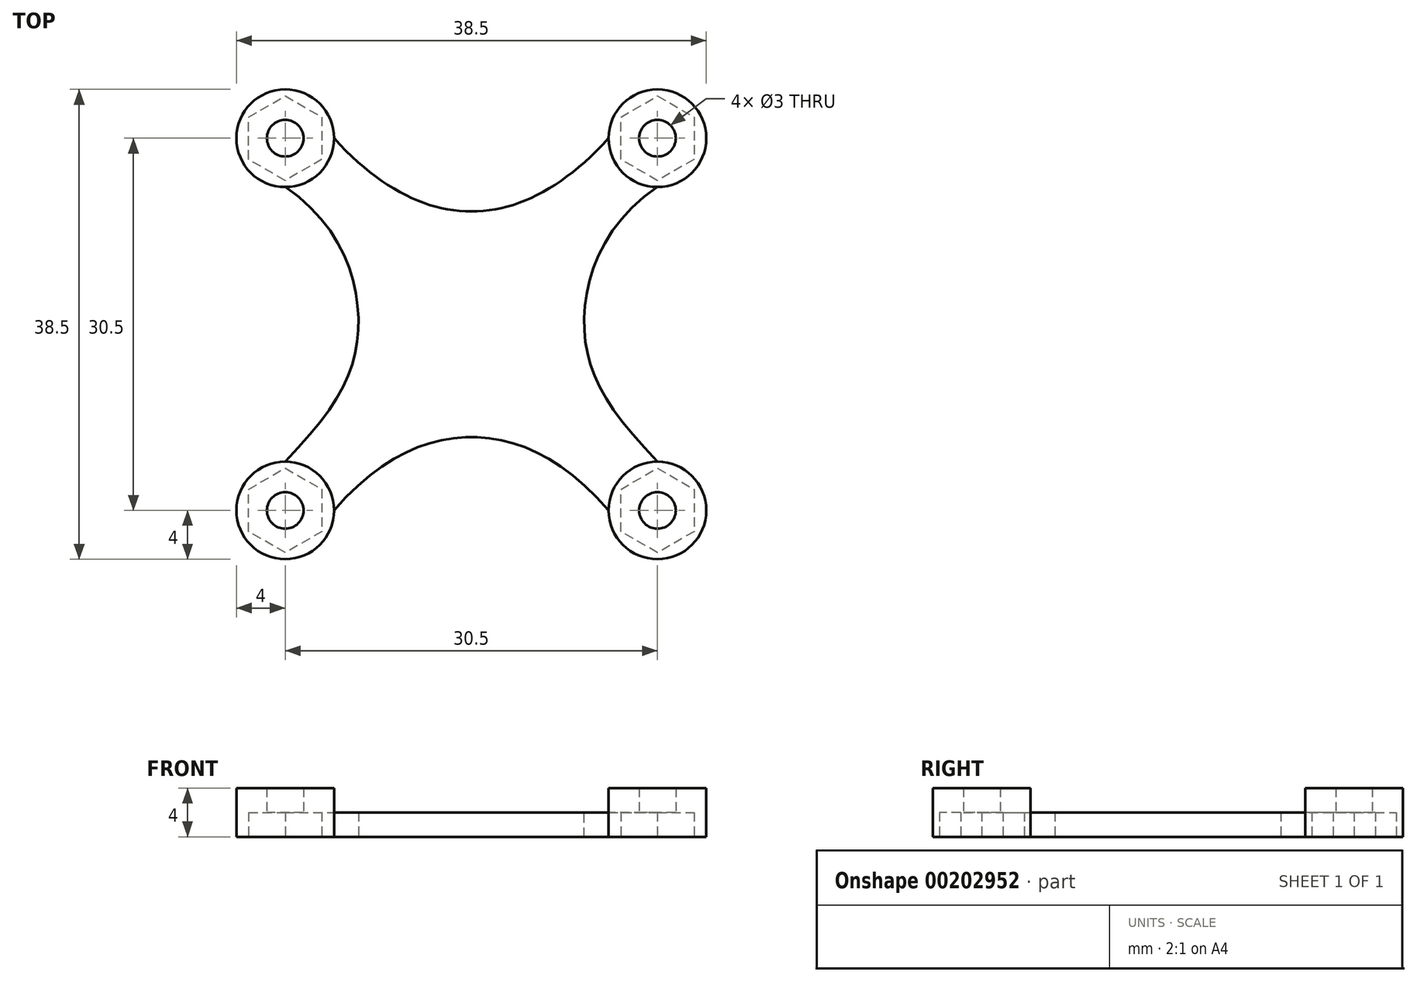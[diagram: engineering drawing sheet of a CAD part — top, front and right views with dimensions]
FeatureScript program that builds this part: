
annotation { "Feature Type Name" : "Feature", "Feature Type Description" : "" }
export const myFeature = defineFeature(function(context is Context, id is Id, definition is map)
    precondition{}
    {
        {
            var Q0;
            Q0=qCreatedBy(makeId("Top.planeOp"),FACE);
            var sketch = newSketch(context, id + "F0", { "sketchPlane" : qUnion([Q0])});
            skCircle(sketch, "E0", {"center": v(0, 0) * mm, "radius": 1.5 * mm});
            skCircle(sketch, "E1.0.1.0", {"center": v(0, 30.5) * mm, "radius": 1.5 * mm});
            skCircle(sketch, "E1.1.0.0", {"center": v(30.5, 0) * mm, "radius": 1.5 * mm});
            skCircle(sketch, "E1.1.1.0", {"center": v(30.5, 30.5) * mm, "radius": 1.5 * mm});
            skCircle(sketch, "E2", {"center": v(0, 0) * mm, "radius": 4 * mm});
            skCircle(sketch, "E3.0.1.0", {"center": v(0, 30.5) * mm, "radius": 4 * mm});
            skCircle(sketch, "E3.1.0.0", {"center": v(30.5, 0) * mm, "radius": 4 * mm});
            skCircle(sketch, "E3.1.1.0", {"center": v(30.5, 30.5) * mm, "radius": 4 * mm});
            skCircle(sketch, "E4.cCircle", {"center": v(0, 0) * mm, "radius": 3 * mm});
            skLineSegment(sketch, "E4.0", {"start": v(3, 1.73) * mm, "end": v(3, -1.73) * mm});
            skLineSegment(sketch, "E4.1", {"start": v(3, -1.73) * mm, "end": v(0, -3.46) * mm});
            skLineSegment(sketch, "E4.2", {"start": v(0, -3.46) * mm, "end": v(-3, -1.73) * mm});
            skLineSegment(sketch, "E4.3", {"start": v(-3, -1.73) * mm, "end": v(-3, 1.73) * mm});
            skLineSegment(sketch, "E4.4", {"start": v(-3, 1.73) * mm, "end": v(0, 3.46) * mm});
            skLineSegment(sketch, "E4.5", {"start": v(0, 3.46) * mm, "end": v(3, 1.73) * mm});
            skPoint(sketch, "E4.0.midPoint", {"position": v(3, 0) * mm});
            skLineSegment(sketch, "E5.0.1.0", {"start": v(0, 33.96) * mm, "end": v(3, 32.23) * mm});
            skLineSegment(sketch, "E5.0.1.1", {"start": v(3, 32.23) * mm, "end": v(3, 28.77) * mm});
            skLineSegment(sketch, "E5.0.1.2", {"start": v(3, 28.77) * mm, "end": v(0, 27.04) * mm});
            skLineSegment(sketch, "E5.0.1.3", {"start": v(0, 27.04) * mm, "end": v(-3, 28.77) * mm});
            skLineSegment(sketch, "E5.0.1.4", {"start": v(-3, 28.77) * mm, "end": v(-3, 32.23) * mm});
            skLineSegment(sketch, "E5.0.1.5", {"start": v(-3, 32.23) * mm, "end": v(0, 33.96) * mm});
            skLineSegment(sketch, "E5.1.0.0", {"start": v(30.5, 3.46) * mm, "end": v(33.5, 1.73) * mm});
            skLineSegment(sketch, "E5.1.0.1", {"start": v(33.5, 1.73) * mm, "end": v(33.5, -1.73) * mm});
            skLineSegment(sketch, "E5.1.0.2", {"start": v(33.5, -1.73) * mm, "end": v(30.5, -3.46) * mm});
            skLineSegment(sketch, "E5.1.0.3", {"start": v(30.5, -3.46) * mm, "end": v(27.5, -1.73) * mm});
            skLineSegment(sketch, "E5.1.0.4", {"start": v(27.5, -1.73) * mm, "end": v(27.5, 1.73) * mm});
            skLineSegment(sketch, "E5.1.0.5", {"start": v(27.5, 1.73) * mm, "end": v(30.5, 3.46) * mm});
            skLineSegment(sketch, "E5.1.1.0", {"start": v(30.5, 33.96) * mm, "end": v(33.5, 32.23) * mm});
            skLineSegment(sketch, "E5.1.1.1", {"start": v(33.5, 32.23) * mm, "end": v(33.5, 28.77) * mm});
            skLineSegment(sketch, "E5.1.1.2", {"start": v(33.5, 28.77) * mm, "end": v(30.5, 27.04) * mm});
            skLineSegment(sketch, "E5.1.1.3", {"start": v(30.5, 27.04) * mm, "end": v(27.5, 28.77) * mm});
            skLineSegment(sketch, "E5.1.1.4", {"start": v(27.5, 28.77) * mm, "end": v(27.5, 32.23) * mm});
            skLineSegment(sketch, "E5.1.1.5", {"start": v(27.5, 32.23) * mm, "end": v(30.5, 33.96) * mm});
            skFitSpline(sketch, "E6", {"points": [v(0, 26.5) * mm, v(6, 15.25) * mm, v(0, 4) * mm], "startDerivative": vector(27.04, -18) * mm, "endDerivative": vector(-26.01, -26.83) * mm});
            skLineSegment(sketch, "E7", {"start": v(15.25, 26.3) * mm, "end": v(15.25, 6.91) * mm});
            skFitSpline(sketch, "E8.MirrorCS", {"points": [v(30.5, 26.5) * mm, v(24.5, 15.25) * mm, v(30.5, 4) * mm], "startDerivative": vector(-27.04, -18) * mm, "endDerivative": vector(26.01, -26.83) * mm});
            skFitSpline(sketch, "E9", {"points": [v(0, 30.5) * mm, v(30.5, 30.5) * mm], "startDerivative": vector(30.5, 0) * mm, "endDerivative": vector(30.5, 0) * mm, "construction": true});
            skFitSpline(sketch, "E10", {"points": [v(0, 0) * mm, v(30.5, 0) * mm], "startDerivative": vector(30.5, 0) * mm, "endDerivative": vector(30.5, 0) * mm, "construction": true});
            skFitSpline(sketch, "E11", {"points": [v(4, 30.5) * mm, v(15.25, 24.5) * mm, v(26.5, 30.5) * mm], "startDerivative": vector(22.5, -24.63) * mm, "endDerivative": vector(22.5, 24.63) * mm});
            skFitSpline(sketch, "E12", {"points": [v(4, 0) * mm, v(15.25, 6) * mm, v(26.5, 0) * mm], "startDerivative": vector(22.5, 25.9) * mm, "endDerivative": vector(22.5, -25.9) * mm});
            skSolve(sketch);
        }
        {
            var Q0;
            Q0 = qSketchRegion(id + "F0", true);
            extrude(context, id + "F1", {"entities" : qUnion([Q0]), "depth" : 2 * mm});
        }
        {
            var Q0;
            Q0=makeQuery(id+"F0.imprint","IMPRINT",FACE,{"disambiguationData":[TD([[makeQuery(id+"F0.imprint","IMPRINT",EDGE,{"derivedFrom":sQuery(id+"F0.wireOp",EDGE,"E5.0.1.0")}),1.0]])]});
            var Q1;
            Q1=makeQuery(id+"F0.imprint","IMPRINT",FACE,{"disambiguationData":[TD([[makeQuery(id+"F0.imprint","IMPRINT",EDGE,{"derivedFrom":sQuery(id+"F0.wireOp",EDGE,"E5.1.1.0")}),1.0]])]});
            var Q2;
            Q2=makeQuery(id+"F0.imprint","IMPRINT",FACE,{"disambiguationData":[TD([[makeQuery(id+"F0.imprint","IMPRINT",EDGE,{"derivedFrom":sQuery(id+"F0.wireOp",EDGE,"E5.1.0.0")}),1.0]])]});
            var Q3;
            {var subQ13=sQuery(id+"F0.wireOp",EDGE,"E2");var subQ14=makeQuery(id+"F0.imprint","INTERSECT",VERTEX,{"derivedFrom":[subQ13,sQuery(id+"F0.wireOp",EDGE,"E6")]});Q3=makeQuery(id+"F0.imprint","IMPRINT",FACE,{"disambiguationData":[TD([[makeQuery(id+"F0.imprint","IMPRINT",EDGE,{"disambiguationData":[TD([[subQ14,1.0]])],"derivedFrom":subQ13}),1.0]])]});}
            extrude(context, id + "F2", {"entities" : qUnion([Q0, Q1, Q2, Q3]), "operationType" : NewBodyOperationType.ADD, "depth" : 4 * mm});
        }
        {
            var Q0;
            Q0=makeQuery(id+"F0.imprint","IMPRINT",FACE,{"disambiguationData":[TD([[makeQuery(id+"F0.imprint","IMPRINT",EDGE,{"derivedFrom":sQuery(id+"F0.wireOp",EDGE,"E0")}),-1.0]])]});
            var Q1;
            {var subQ0=sQuery(id+"F0.wireOp",EDGE,"E4.4");var subQ1=sQuery(id+"F0.wireOp",EDGE,"E4.cCircle");var subQ2=makeQuery(id+"F0.imprint","INTERSECT",VERTEX,{"derivedFrom":[subQ1,subQ0]});Q1=makeQuery(id+"F0.imprint","IMPRINT",FACE,{"disambiguationData":[TD([[makeQuery(id+"F0.imprint","IMPRINT",EDGE,{"disambiguationData":[TD([[subQ2,-1.0]])],"derivedFrom":subQ1}),-1.0]])]});}
            var Q2;
            {var subQ0=sQuery(id+"F0.wireOp",EDGE,"E4.5");var subQ1=sQuery(id+"F0.wireOp",EDGE,"E4.cCircle");var subQ2=makeQuery(id+"F0.imprint","INTERSECT",VERTEX,{"derivedFrom":[subQ1,subQ0]});Q2=makeQuery(id+"F0.imprint","IMPRINT",FACE,{"disambiguationData":[TD([[makeQuery(id+"F0.imprint","IMPRINT",EDGE,{"disambiguationData":[TD([[subQ2,1.0]])],"derivedFrom":subQ1}),-1.0]])]});}
            var Q3;
            {var subQ0=sQuery(id+"F0.wireOp",EDGE,"E4.0");var subQ1=sQuery(id+"F0.wireOp",EDGE,"E4.cCircle");var subQ2=makeQuery(id+"F0.imprint","INTERSECT",VERTEX,{"derivedFrom":[subQ1,subQ0]});Q3=makeQuery(id+"F0.imprint","IMPRINT",FACE,{"disambiguationData":[TD([[makeQuery(id+"F0.imprint","IMPRINT",EDGE,{"disambiguationData":[TD([[subQ2,1.0]])],"derivedFrom":subQ1}),-1.0]])]});}
            var Q4;
            {var subQ0=sQuery(id+"F0.wireOp",EDGE,"E4.3");var subQ1=sQuery(id+"F0.wireOp",EDGE,"E4.cCircle");var subQ2=makeQuery(id+"F0.imprint","INTERSECT",VERTEX,{"derivedFrom":[subQ1,subQ0]});Q4=makeQuery(id+"F0.imprint","IMPRINT",FACE,{"disambiguationData":[TD([[makeQuery(id+"F0.imprint","IMPRINT",EDGE,{"disambiguationData":[TD([[subQ2,-1.0]])],"derivedFrom":subQ1}),-1.0]])]});}
            var Q5;
            {var subQ0=sQuery(id+"F0.wireOp",EDGE,"E4.5");var subQ1=sQuery(id+"F0.wireOp",EDGE,"E4.cCircle");var subQ2=makeQuery(id+"F0.imprint","INTERSECT",VERTEX,{"derivedFrom":[subQ1,subQ0]});Q5=makeQuery(id+"F0.imprint","IMPRINT",FACE,{"disambiguationData":[TD([[makeQuery(id+"F0.imprint","IMPRINT",EDGE,{"disambiguationData":[TD([[subQ2,-1.0]])],"derivedFrom":subQ1}),-1.0]])]});}
            var Q6;
            {var subQ0=sQuery(id+"F0.wireOp",EDGE,"E4.2");var subQ1=sQuery(id+"F0.wireOp",EDGE,"E4.cCircle");var subQ2=makeQuery(id+"F0.imprint","INTERSECT",VERTEX,{"derivedFrom":[subQ1,subQ0]});Q6=makeQuery(id+"F0.imprint","IMPRINT",FACE,{"disambiguationData":[TD([[makeQuery(id+"F0.imprint","IMPRINT",EDGE,{"disambiguationData":[TD([[subQ2,-1.0]])],"derivedFrom":subQ1}),-1.0]])]});}
            var Q7;
            Q7=makeQuery(id+"F0.imprint","IMPRINT",FACE,{"disambiguationData":[TD([[makeQuery(id+"F0.imprint","IMPRINT",EDGE,{"derivedFrom":sQuery(id+"F0.wireOp",EDGE,"E1.1.0.0")}),-1.0]])]});
            var Q8;
            Q8=makeQuery(id+"F0.imprint","IMPRINT",FACE,{"disambiguationData":[TD([[makeQuery(id+"F0.imprint","IMPRINT",EDGE,{"derivedFrom":sQuery(id+"F0.wireOp",EDGE,"E1.1.1.0")}),-1.0]])]});
            var Q9;
            Q9=makeQuery(id+"F0.imprint","IMPRINT",FACE,{"disambiguationData":[TD([[makeQuery(id+"F0.imprint","IMPRINT",EDGE,{"derivedFrom":sQuery(id+"F0.wireOp",EDGE,"E1.0.1.0")}),-1.0]])]});
            extrude(context, id + "F3", {"entities" : qUnion([Q0, Q1, Q2, Q3, Q4, Q5, Q6, Q7, Q8, Q9]), "operationType" : NewBodyOperationType.ADD, "depth" : 4 * mm, "hasSecondDirection" : true, "secondDirectionOppositeDirection" : false, "secondDirectionDepth" : 2 * mm});
        }
    });
